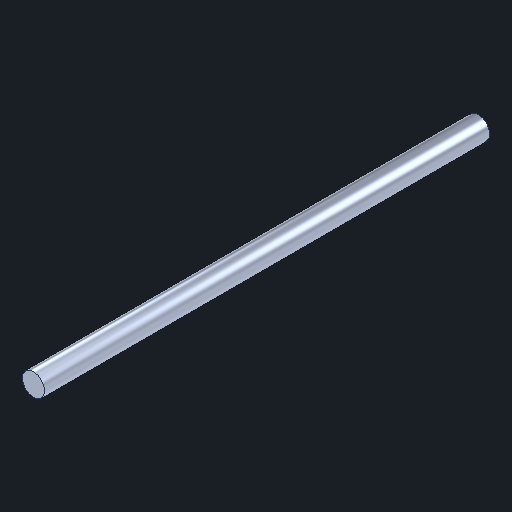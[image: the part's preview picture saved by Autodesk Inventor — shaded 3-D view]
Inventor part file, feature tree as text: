
AUTODESK INVENTOR PART (.ipt)
format: ipt  version: 2024 (Build 280153000, 153)  size: 118,272 bytes
history: native  units: in
note: dims shown in document units (in); Inventor stores cm internally (conversion verified against a paired STEP export)
features: other x2, extrude x2
ambient origin geometry x8: Origin, YZ Plane, XZ Plane, XY Plane, X Axis, Y Axis, Z Axis, Center Point
bodies: Body1 (feature_tree)
feature tree (4):
  other  "Pin 5.ipt"
  extrude  "Extrude1::Pin 5.ipt"  Depth=0.3937in
  other  "TaggingFeature1"
  extrude  "Extrude1"  [1 undecoded]
note: 1 required parameter value undecoded (feature->parameter linkage not recoverable at this tier; creation-order binding heuristic only, values carry confidence <= 0.55)
